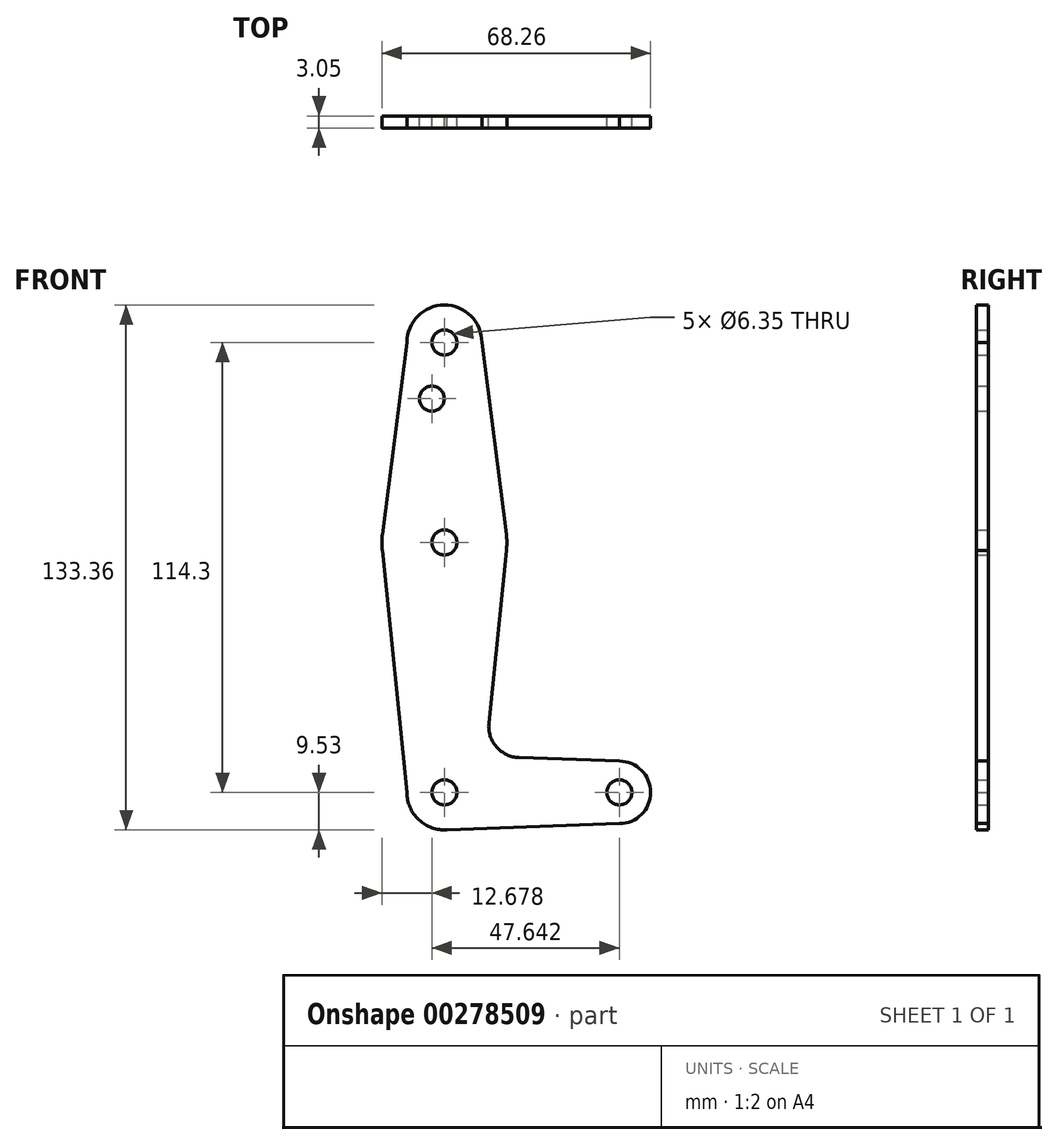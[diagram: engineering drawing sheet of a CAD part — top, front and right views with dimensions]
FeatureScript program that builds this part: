
annotation { "Feature Type Name" : "Feature", "Feature Type Description" : "" }
export const myFeature = defineFeature(function(context is Context, id is Id, definition is map)
    precondition{}
    {
        {
            var Q0;
            Q0=qCreatedBy(makeId("Front.planeOp"),FACE);
            var sketch = newSketch(context, id + "F0", { "sketchPlane" : qUnion([Q0])});
            skCircle(sketch, "E0", {"center": v(0, 114.3) * mm, "radius": 9.53 * mm});
            skCircle(sketch, "E1", {"center": v(0, 0) * mm, "radius": 9.53 * mm});
            skLineSegment(sketch, "E2", {"start": v(0, 0) * mm, "end": v(44.45, 0) * mm, "construction": true});
            skCircle(sketch, "E3", {"center": v(0, 63.5) * mm, "radius": 15.88 * mm});
            skCircle(sketch, "E4", {"center": v(44.45, 0) * mm, "radius": 7.94 * mm});
            skLineSegment(sketch, "E5", {"start": v(0, 114.3) * mm, "end": v(0, 0) * mm, "construction": true});
            skLineSegment(sketch, "E6", {"start": v(-9.52, 114.3) * mm, "end": v(-15.75, 65.5) * mm});
            skLineSegment(sketch, "E7", {"start": v(9.52, 114.3) * mm, "end": v(15.75, 65.5) * mm});
            skLineSegment(sketch, "E8", {"start": v(11.3, 17.6) * mm, "end": v(15.75, 61.5) * mm});
            skLineSegment(sketch, "E9", {"start": v(-9.52, 0) * mm, "end": v(-15.75, 61.5) * mm});
            skLineSegment(sketch, "E10", {"start": v(18.93, 8.85) * mm, "end": v(44.45, 7.94) * mm});
            skLineSegment(sketch, "E11", {"start": v(0, -9.53) * mm, "end": v(44.45, -7.94) * mm});
            skCircle(sketch, "E12", {"center": v(0, 63.5) * mm, "radius": 3.18 * mm});
            skCircle(sketch, "E13", {"center": v(0, 114.3) * mm, "radius": 3.18 * mm});
            skCircle(sketch, "E14", {"center": v(0, 0) * mm, "radius": 3.18 * mm});
            skCircle(sketch, "E15", {"center": v(44.45, 0) * mm, "radius": 3.18 * mm});
            skCircle(sketch, "E16", {"center": v(-3.2, 100.03) * mm, "radius": 3.18 * mm});
            skArc(sketch, "E17.filletArc", {"start": v(11.3, 17.6) * mm, "mid": v(13.22, 11.57) * mm, "end": v(18.93, 8.85) * mm});
            skSolve(sketch);
        }
        {
            var Q0;
            Q0 = qSketchRegion(id + "F0", true);
            var Q1;
            {var subQ1=sQuery(id+"F0.wireOp",EDGE,"E6");Q1=makeQuery(id+"F0.imprint","IMPRINT",FACE,{"disambiguationData":[TD([[makeQuery(id+"F0.imprint","IMPRINT",EDGE,{"derivedFrom":subQ1}),1.0]])]});}
            extrude(context, id + "F1", {"entities" : qUnion([Q0, Q1]), "depth" : 3.05 * mm});
        }
    });
